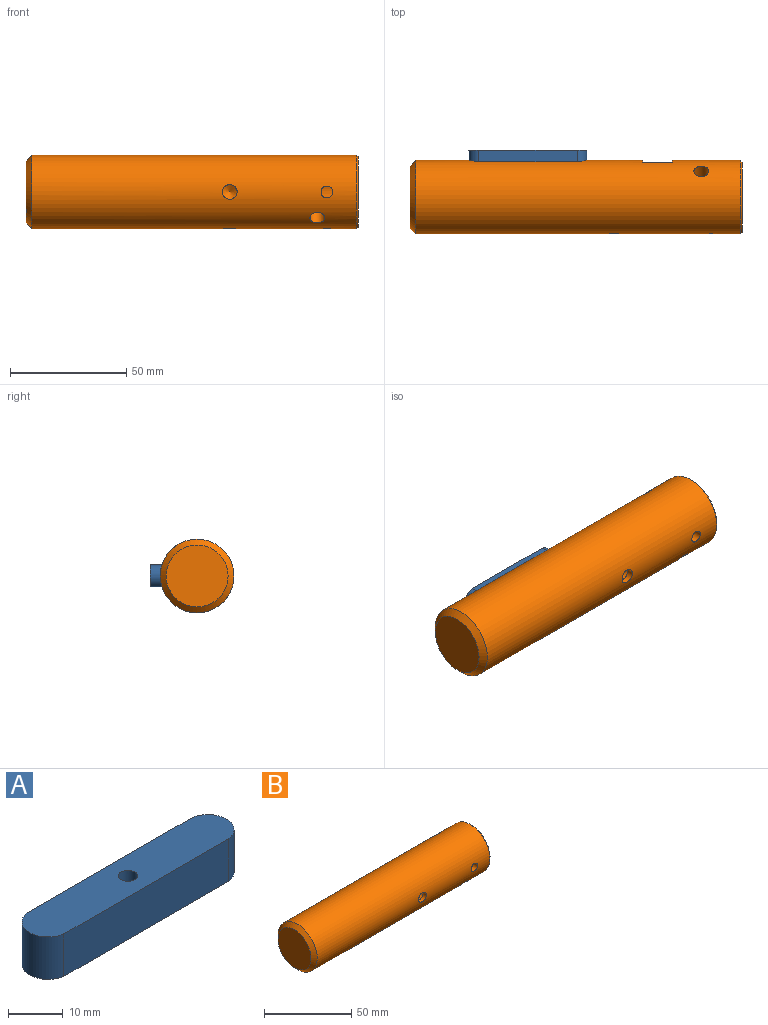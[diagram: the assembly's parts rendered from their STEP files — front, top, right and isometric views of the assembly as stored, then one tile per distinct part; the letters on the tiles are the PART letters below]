
ASSEMBLY  parts=2 mates=1
PART A: 9 faces, bbox 50.8x9.5x9.5 mm
  f0: plane 42.57x9.49mm, normal (0,1,0), area 403.8mm2, adj f1,f3,f4,f5
  f1: cylinder r=4.78mm len=9.49mm, axis (0,0,-1), area 129.9mm2, adj f0,f2,f4,f5
  f2: plane 42.57x9.49mm, normal (0,-1,0), area 403.8mm2, adj f1,f3,f4,f5
  f3: cylinder r=4.78mm len=9.49mm, axis (0,0,-1), area 129.9mm2, adj f0,f2,f4,f5
  f4: plane 50.8x9.47mm, normal (0,0,1), area 453.1mm2, adj f0,f1,f2,f3,f6
  f5: plane 50.8x9.47mm, normal (0,0,-1), area 413mm2, adj f0,f1,f2,f3,f8
  f6: cylinder r=1.73mm len=5.32mm, axis (0,0,-1), area 57.7mm2, adj f4,f7
  f7: plane 7.94x7.94mm, normal (0,0,-1), area 40.1mm2, adj f6,f8
  f8: cylinder r=3.97mm len=7.94mm, axis (0,0,-1), area 103.9mm2, adj f5,f7
PART B: 65 faces, bbox 143x31.8x31.8 mm
  f0: cylinder r=15.88mm len=139.7mm, axis (-1,0,0), area 13151.6mm2, adj f2,f3,f6,f7,f8,f9,f11,f12
  f1: cylinder r=9.53mm len=25.4mm, axis (1,0,0), area 1414.5mm2, adj f3,f4,f12,f13,f61,f62
  f2: plane 12.7x11.18mm, normal (0,1,0), area 105.7mm2, adj f0,f14,f15,f16,f17,f18,f19,f20
  f3: cylinder r=3.17mm len=9.37mm, axis (0,0.71,0.71), area 128.9mm2, adj f0,f1
  f4: plane 30.23x30.23mm, normal (1,0,0), area 432.5mm2, adj f1,f56
  f5: plane 26.67x26.67mm, normal (-1,0,0), area 558.6mm2, adj f11
  f6: plane 42.57x4.36mm, normal (0,0,-1), area 185.5mm2, adj f0,f7,f9,f10
  f7: cylinder r=4.78mm len=9.47mm, axis (0,1,0), area 65mm2, adj f0,f6,f8,f10
  f8: plane 42.57x4.36mm, normal (0,0,1), area 185.5mm2, adj f0,f7,f9,f10
  f9: cylinder r=4.78mm len=9.47mm, axis (0,1,0), area 65mm2, adj f0,f6,f8,f10
  f10: plane 50.8x9.47mm, normal (0,1,0), area 453.1mm2, adj f6,f7,f8,f9,f64
  f11: cone r=15.88mm half-angle=45deg, axis (1,0,0), area 329.6mm2, adj f0,f5
  f12: cylinder r=3.17mm len=9.37mm, axis (0,0.71,0.71), area 128.9mm2, adj f0,f1
  f13: plane 19.05x19.05mm, normal (1,0,0), area 285mm2, adj f1
  f14: plane 11.18x1.02mm, normal (-1,0,0), area 7.6mm2, adj f0,f2
  f15: plane 11.18x1.02mm, normal (1,0,0), area 7.6mm2, adj f0,f2
  f16: plane 0.92x0.25mm, normal (0,0,1), area 0.2mm2, adj f2,f17,f35,f36
  f17: extruded ~2.14x0.36mm, area 0.6mm2, adj f2,f16,f18,f36
  f18: extruded ~2.03x0.57mm, area 0.5mm2, adj f2,f17,f19,f36
  f19: extruded ~1.56x0.72mm, area 0.5mm2, adj f2,f18,f20,f36
  f20: extruded ~1.24x0.43mm, area 0.3mm2, adj f2,f19,f21,f36
  f21: extruded ~1.7x0.94mm, area 0.5mm2, adj f2,f20,f22,f36
  f22: extruded ~1.4x0.69mm, area 0.4mm2, adj f2,f21,f23,f36
  f23: extruded ~0.85x0.34mm, area 0.2mm2, adj f2,f22,f24,f36
  f24: extruded ~1.51x1.08mm, area 0.5mm2, adj f2,f23,f25,f36
  f25: extruded ~1.86x0.4mm, area 0.5mm2, adj f2,f24,f26,f36
  f26: plane 0.85x0.33mm, normal (0.36,0,-0.93), area 0.2mm2, adj f2,f25,f27,f36
  f27: extruded ~2.15x0.4mm, area 0.6mm2, adj f2,f26,f28,f36
  f28: extruded ~1.82x0.51mm, area 0.5mm2, adj f2,f27,f29,f36
  f29: extruded ~1.41x0.66mm, area 0.4mm2, adj f2,f28,f30,f36
  f30: extruded ~1.36x0.47mm, area 0.4mm2, adj f2,f29,f31,f36
  f31: extruded ~1.54x0.9mm, area 0.5mm2, adj f2,f30,f32,f36
  f32: extruded ~1.48x0.69mm, area 0.4mm2, adj f2,f31,f33,f36
  f33: extruded ~0.83x0.36mm, area 0.2mm2, adj f2,f32,f34,f36
  f34: extruded ~1.81x1.24mm, area 0.6mm2, adj f2,f33,f35,f36
  f35: extruded ~2.14x0.44mm, area 0.6mm2, adj f2,f16,f34,f36
  f36: plane 7.77x4.89mm, normal (0,1,0), area 14.4mm2, adj f16,f17,f18,f19,f20,f21,f22,f23
  f37: plane 0.8x0.25mm, normal (1,0,0), area 0.2mm2, adj f2,f38,f54,f55
  f38: plane 6.61x1.44mm, normal (0.21,0,-0.98), area 1.7mm2, adj f2,f37,f39,f55
  f39: plane 0.25x0.04mm, normal (1,0,0), area 0mm2, adj f2,f38,f40,f55
  f40: extruded ~2.1x0.25mm, area 0.5mm2, adj f2,f39,f41,f55
  f41: plane 4.52x0.25mm, normal (0,0,1), area 1.1mm2, adj f2,f40,f42,f55
  f42: plane 0.78x0.25mm, normal (1,0,0), area 0.2mm2, adj f2,f41,f43,f55
  f43: plane 7.56x0.25mm, normal (0,0,-1), area 1.9mm2, adj f2,f42,f44,f55
  f44: plane 1.28x0.25mm, normal (-1,0,0), area 0.3mm2, adj f2,f43,f45,f55
  f45: plane 6.16x1.28mm, normal (-0.2,0,0.98), area 1.6mm2, adj f2,f44,f46,f55
  f46: plane 0.25x0.03mm, normal (-1,0,0), area 0mm2, adj f2,f45,f47,f55
  f47: plane 6.16x1.29mm, normal (-0.21,0,-0.98), area 1.6mm2, adj f2,f46,f48,f55
  f48: plane 1.3x0.25mm, normal (-1,0,0), area 0.3mm2, adj f2,f47,f49,f55
  f49: plane 7.56x0.25mm, normal (0,0,1), area 1.9mm2, adj f2,f48,f50,f55
  f50: plane 0.79x0.25mm, normal (1,0,0), area 0.2mm2, adj f2,f49,f51,f55
  f51: plane 4.58x0.25mm, normal (0,0,-1), area 1.2mm2, adj f2,f50,f52,f55
  f52: extruded ~2.02x0.25mm, area 0.5mm2, adj f2,f51,f53,f55
  f53: plane 0.25x0.04mm, normal (1,0,0), area 0mm2, adj f2,f52,f54,f55
  f54: plane 6.6x1.46mm, normal (0.22,0,0.98), area 1.7mm2, adj f2,f37,f53,f55
  f55: plane 7.56x5.18mm, normal (0,1,0), area 21.9mm2, adj f37,f38,f39,f40,f41,f42,f43,f44
  f56: cone r=15.11mm half-angle=45deg, axis (-1,0,0), area 104.9mm2, adj f0,f4
  f57: cylinder r=3.17mm len=6.35mm, axis (0,0,-1), area 53.9mm2, adj f0,f58
  f58: cone r=0mm half-angle=59deg, axis (0,0,-1), area 36.9mm2, adj f57
  f59: cylinder r=3.17mm len=6.35mm, axis (0,-1,0), area 53.9mm2, adj f0,f60
  f60: cone r=0mm half-angle=59deg, axis (0,-1,0), area 36.9mm2, adj f59
  f61: cylinder r=2.55mm len=6.7mm, axis (0,0,-1), area 103mm2, adj f0,f1
  f62: cylinder r=2.55mm len=6.7mm, axis (0,-1,0), area 103mm2, adj f0,f1
  f63: cone r=0mm half-angle=59deg, axis (0,1,0), area 10.9mm2, adj f64
  f64: cylinder r=1.73mm len=11.59mm, axis (0,1,0), area 125.8mm2, adj f10,f63
PLACE A rot(axis=(1,0,0),90deg) t=(-20.68,20.32,0.04)mm
PLACE B t=(-71.48,0.04,0.04)mm
MATE fastened A.f3 <-> B.f9  axis (0,-1,0) through (-0.07,10.84,0.04)mm
